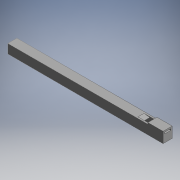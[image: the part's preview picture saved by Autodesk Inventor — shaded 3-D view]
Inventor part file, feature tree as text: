
AUTODESK INVENTOR PART (.ipt)
format: ipt  version: 2018 (Build 220112000, 112)  size: 134,656 bytes
history: native  units: in
note: dims shown in document units (in); Inventor stores cm internally (conversion verified against a paired STEP export)
features: extrude x3, other x3, plane x1
ambient origin geometry x8: Origin, YZ Plane, XZ Plane, XY Plane, X Axis, Y Axis, Z Axis, Center Point
bodies: Body1 (feature_tree)
feature tree (7):
  extrude  "Tube"  TaperAngle=0.0deg  [1 undecoded]
  extrude  "Extrusion6"  TaperAngle=0.0deg  [1 undecoded]
  plane  "Work Plane1"
  extrude  "Edge Cut and Slit"  Depth=0.315in
  other  "Tube Base Sketch"
  other  "Cap Sketch"
  other  "Edge Cut and Slit Sketch"
note: 2 required parameter values undecoded (feature->parameter linkage not recoverable at this tier; creation-order binding heuristic only, values carry confidence <= 0.55)
